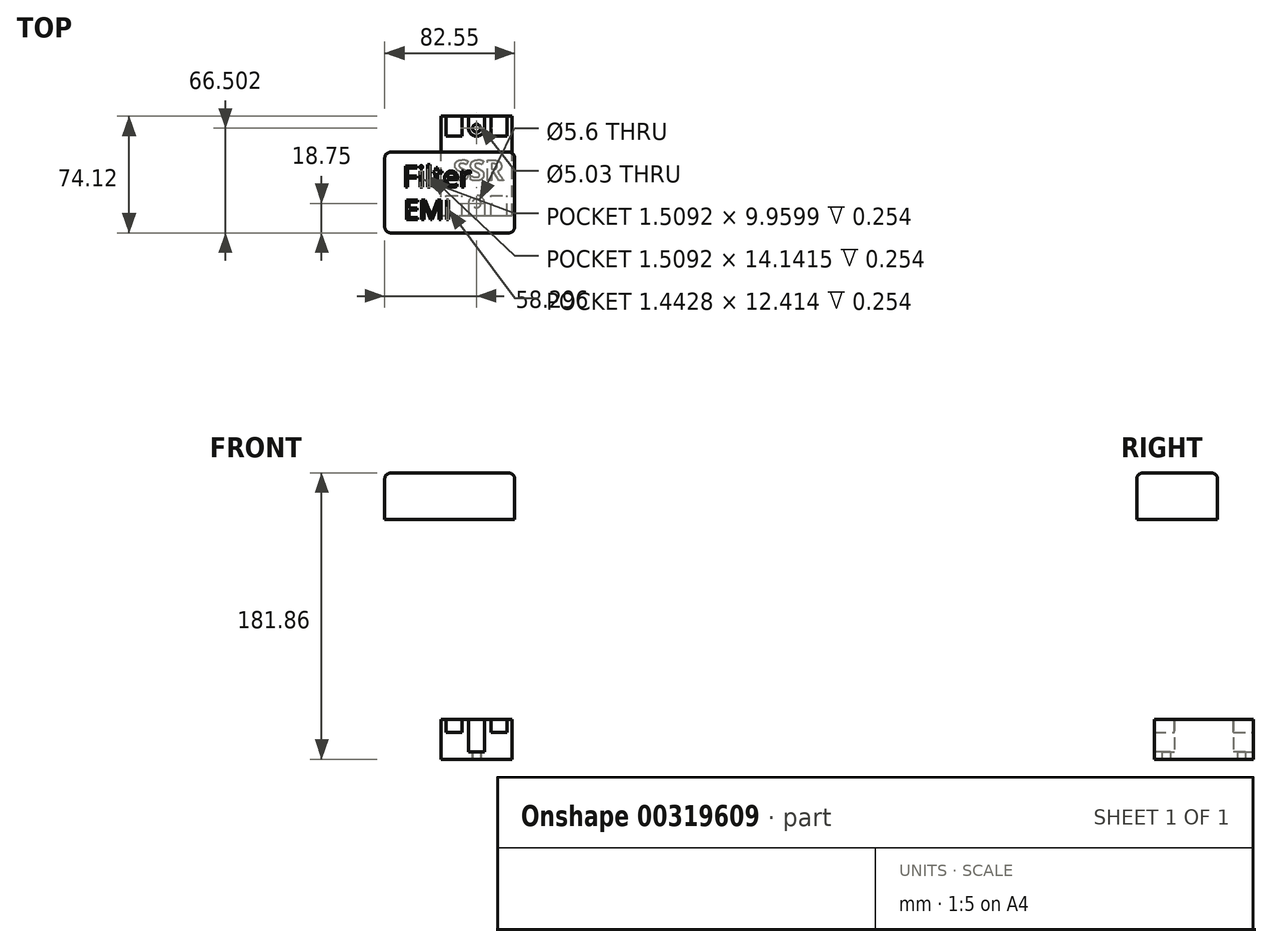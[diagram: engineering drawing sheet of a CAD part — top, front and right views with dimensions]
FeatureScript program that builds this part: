
annotation { "Feature Type Name" : "Feature", "Feature Type Description" : "" }
export const myFeature = defineFeature(function(context is Context, id is Id, definition is map)
    precondition{}
    {
        {
            var Q0;
            Q0=qCreatedBy(makeId("Top.planeOp"),FACE);
            var sketch = newSketch(context, id + "F0", { "sketchPlane" : qUnion([Q0])});
            skLineSegment(sketch, "E0.bottom", {"start": v(0, 0) * mm, "end": v(45.21, 0) * mm});
            skLineSegment(sketch, "E0.top", {"start": v(0, 63) * mm, "end": v(45.21, 63) * mm});
            skLineSegment(sketch, "E0.left", {"start": v(0, 0) * mm, "end": v(0, 63) * mm});
            skLineSegment(sketch, "E0.right", {"start": v(45.21, 0) * mm, "end": v(45.21, 63) * mm});
            skLineSegment(sketch, "E1", {"start": v(22.6, 63) * mm, "end": v(22.6, 0) * mm, "construction": true});
            skLineSegment(sketch, "E2.0", {"start": v(0, 55.37) * mm, "end": v(45.21, 55.37) * mm, "construction": true});
            skLineSegment(sketch, "E3.0", {"start": v(0, 7.62) * mm, "end": v(45.21, 7.62) * mm, "construction": true});
            skArc(sketch, "E4", {"start": v(27.69, 7.62) * mm, "mid": v(22.6, 12.7) * mm, "end": v(17.53, 7.62) * mm});
            skArc(sketch, "E5", {"start": v(17.53, 55.37) * mm, "mid": v(22.6, 50.3) * mm, "end": v(27.69, 55.37) * mm});
            skLineSegment(sketch, "E6", {"start": v(27.69, 55.37) * mm, "end": v(27.69, 63) * mm});
            skLineSegment(sketch, "E7", {"start": v(17.53, 55.37) * mm, "end": v(17.53, 63) * mm});
            skLineSegment(sketch, "E8", {"start": v(27.69, 7.62) * mm, "end": v(27.69, 0) * mm});
            skLineSegment(sketch, "E9", {"start": v(17.53, 7.62) * mm, "end": v(17.53, 0) * mm});
            skCircle(sketch, "E10", {"center": v(22.6, 55.37) * mm, "radius": 2.51 * mm});
            skCircle(sketch, "E11", {"center": v(22.6, 7.62) * mm, "radius": 2.8 * mm});
            skSolve(sketch);
        }
        {
            var Q0;
            {var subQ2=sQuery(id+"F0.wireOp",EDGE,"E0.left");Q0=makeQuery(id+"F0.imprint","IMPRINT",FACE,{"disambiguationData":[TD([[makeQuery(id+"F0.imprint","IMPRINT",EDGE,{"derivedFrom":subQ2}),-1.0]])]});}
            extrude(context, id + "F1", {"entities" : qUnion([Q0]), "depth" : 25.4 * mm});
        }
        {
            var Q0;
            Q0=makeQuery(id+"F0.imprint","IMPRINT",FACE,{"disambiguationData":[TD([[makeQuery(id+"F0.imprint","IMPRINT",EDGE,{"derivedFrom":sQuery(id+"F0.wireOp",EDGE,"E4")}),1.0]])]});
            var Q1;
            Q1=makeQuery(id+"F0.imprint","IMPRINT",FACE,{"disambiguationData":[TD([[makeQuery(id+"F0.imprint","IMPRINT",EDGE,{"derivedFrom":sQuery(id+"F0.wireOp",EDGE,"E5")}),1.0]])]});
            extrude(context, id + "F2", {"entities" : qUnion([Q0, Q1]), "operationType" : NewBodyOperationType.ADD, "depth" : 4.57 * mm});
        }
        {
            var Q0;
            Q0=makeQuery(id+"F1.opExtrude","CAP_FACE",FACE,{"disambiguationData":[OSD([sQuery(id+"F0.wireOp",EDGE,"E0.bottom"),sQuery(id+"F0.wireOp",EDGE,"E0.top"),sQuery(id+"F0.wireOp",EDGE,"E0.left"),sQuery(id+"F0.wireOp",EDGE,"E0.right"),sQuery(id+"F0.wireOp",EDGE,"E4"),sQuery(id+"F0.wireOp",EDGE,"E5"),sQuery(id+"F0.wireOp",EDGE,"E6"),sQuery(id+"F0.wireOp",EDGE,"E7"),sQuery(id+"F0.wireOp",EDGE,"E8"),sQuery(id+"F0.wireOp",EDGE,"E9")])],"isStart":false});
            var sketch = newSketch(context, id + "F3", { "sketchPlane" : qUnion([Q0])});
            skLineSegment(sketch, "E12.0", {"start": v(45.21, 0) * mm, "end": v(45.21, 63) * mm});
            skLineSegment(sketch, "E13.0", {"start": v(0, 0) * mm, "end": v(0, 63) * mm});
            skLineSegment(sketch, "E14.0", {"start": v(0, 0) * mm, "end": v(17.53, 0) * mm});
            skLineSegment(sketch, "E15.0", {"start": v(27.69, 0) * mm, "end": v(45.21, 0) * mm});
            skLineSegment(sketch, "E16.0", {"start": v(27.69, 63) * mm, "end": v(45.21, 63) * mm});
            skLineSegment(sketch, "E17.0", {"start": v(0, 63) * mm, "end": v(17.53, 63) * mm});
            skLineSegment(sketch, "E18.0", {"start": v(3.3, 0) * mm, "end": v(3.3, 12.7) * mm});
            skLineSegment(sketch, "E19.0", {"start": v(41.91, 0) * mm, "end": v(41.91, 12.7) * mm});
            skLineSegment(sketch, "E20.0", {"start": v(13.46, 0) * mm, "end": v(13.46, 12.7) * mm});
            skLineSegment(sketch, "E21.0", {"start": v(31.75, 0) * mm, "end": v(31.75, 12.7) * mm});
            skLineSegment(sketch, "E22.0", {"start": v(31.75, 12.7) * mm, "end": v(41.91, 12.7) * mm});
            skLineSegment(sketch, "E23.0", {"start": v(3.3, 12.7) * mm, "end": v(13.46, 12.7) * mm});
            skLineSegment(sketch, "E24.0", {"start": v(3.3, 50.3) * mm, "end": v(13.46, 50.3) * mm});
            skLineSegment(sketch, "E25.0", {"start": v(31.75, 50.3) * mm, "end": v(41.9, 50.3) * mm});
            skLineSegment(sketch, "E26.trimOffspring", {"start": v(41.9, 50.3) * mm, "end": v(41.9, 63) * mm});
            skLineSegment(sketch, "E27.trimOffspring", {"start": v(31.75, 50.3) * mm, "end": v(31.75, 63) * mm});
            skLineSegment(sketch, "E28.trimOffspring", {"start": v(13.46, 50.3) * mm, "end": v(13.46, 63) * mm});
            skLineSegment(sketch, "E29.trimOffspring", {"start": v(3.3, 50.3) * mm, "end": v(3.3, 63) * mm});
            skText(sketch, "E30", { "text": "SSR\n", "fontName": "OpenSans-Bold.ttf"});
            const initialGuessF3  = {"E30": [0.00792, 0.02215, 1, 0, 0.01303]};
            skSetInitialGuess(sketch, initialGuessF3);
            skSolve(sketch);
        }
        {
            var Q0;
            {var subQ0=sQuery(id+"F3.wireOp",EDGE,"E19.0");Q0=makeQuery(id+"F3.imprint","IMPRINT",FACE,{"disambiguationData":[TD([[makeQuery(id+"F3.imprint","IMPRINT",EDGE,{"derivedFrom":subQ0}),1.0]])]});}
            var Q1;
            {var subQ0=sQuery(id+"F3.wireOp",EDGE,"E18.0");Q1=makeQuery(id+"F3.imprint","IMPRINT",FACE,{"disambiguationData":[TD([[makeQuery(id+"F3.imprint","IMPRINT",EDGE,{"derivedFrom":subQ0}),-1.0]])]});}
            var Q2;
            Q2=makeQuery(id+"F3.imprint","IMPRINT",FACE,{"disambiguationData":[TD([[makeQuery(id+"F3.imprint","IMPRINT",EDGE,{"derivedFrom":sQuery(id+"F3.wireOp",EDGE,"E24.0")}),1.0]])]});
            var Q3;
            Q3=makeQuery(id+"F3.imprint","IMPRINT",FACE,{"disambiguationData":[TD([[makeQuery(id+"F3.imprint","IMPRINT",EDGE,{"derivedFrom":sQuery(id+"F3.wireOp",EDGE,"E25.0")}),1.0]])]});
            extrude(context, id + "F4", {"entities" : qUnion([Q0, Q1, Q2, Q3]), "operationType" : NewBodyOperationType.REMOVE, "oppositeDirection" : true, "depth" : 8.38 * mm});
        }
        {
            var Q0;
            Q0=makeQuery(id+"F3.imprint","IMPRINT",FACE,{"disambiguationData":[TD([[makeQuery(id+"F3.imprint","IMPRINT",EDGE,{"derivedFrom":sQuery(id+"F3.wireOp",EDGE,"E30.sketch_text.stroke-56")}),-1.0]])]});
            var Q1;
            Q1=makeQuery(id+"F3.imprint","IMPRINT",FACE,{"disambiguationData":[TD([[makeQuery(id+"F3.imprint","IMPRINT",EDGE,{"derivedFrom":sQuery(id+"F3.wireOp",EDGE,"E30.sketch_text.stroke-28")}),-1.0]])]});
            var Q2;
            Q2=makeQuery(id+"F3.imprint","IMPRINT",FACE,{"disambiguationData":[TD([[makeQuery(id+"F3.imprint","IMPRINT",EDGE,{"derivedFrom":sQuery(id+"F3.wireOp",EDGE,"E30.sketch_text.stroke-0")}),-1.0]])]});
            extrude(context, id + "F5", {"entities" : qUnion([Q0, Q1, Q2]), "operationType" : NewBodyOperationType.REMOVE, "oppositeDirection" : true, "depth" : 0.25 * mm});
        }
        {
            var Q0;
            Q0=qCreatedBy(makeId("Top.planeOp"),FACE);
            cPlane(context, id + "F6", {"entities" : qUnion([Q0]), "cplaneType" : CPlaneType.OFFSET, "offset" : 152.4 * mm, "width" : 152.4 * mm, "height" : 152.4 * mm});
        }
        {
            var Q0;
            Q0=qCreatedBy(id+"F6.planeOp",FACE);
            var sketch = newSketch(context, id + "F7", { "sketchPlane" : qUnion([Q0])});
            skLineSegment(sketch, "E31.bottom", {"start": v(-35.69, 40.18) * mm, "end": v(46.86, 40.18) * mm});
            skLineSegment(sketch, "E31.top", {"start": v(-35.69, -11.13) * mm, "end": v(46.86, -11.13) * mm});
            skLineSegment(sketch, "E31.left", {"start": v(-35.69, 40.18) * mm, "end": v(-35.69, -11.13) * mm});
            skLineSegment(sketch, "E31.right", {"start": v(46.86, 40.18) * mm, "end": v(46.86, -11.13) * mm});
            skSolve(sketch);
        }
        {
            var Q0;
            Q0=makeQuery(id+"F7.imprint","IMPRINT",FACE,{"disambiguationData":[TD([[makeQuery(id+"F7.imprint","IMPRINT",EDGE,{"derivedFrom":sQuery(id+"F7.wireOp",EDGE,"E31.bottom")}),-1.0]])]});
            extrude(context, id + "F8", {"entities" : qUnion([Q0]), "depth" : 29.46 * mm});
        }
        {
            var Q0;
            Q0=makeQuery(id+"F8.opExtrude","CAP_EDGE",EDGE,{"disambiguationData":[OSD([sQuery(id+"F7.wireOp",EDGE,"E31.top")])],"isStart":false});
            var Q1;
            Q1=makeQuery(id+"F8.opExtrude","CAP_EDGE",EDGE,{"disambiguationData":[OSD([sQuery(id+"F7.wireOp",EDGE,"E31.right")])],"isStart":false});
            var Q2;
            Q2=makeQuery(id+"F8.opExtrude","CAP_EDGE",EDGE,{"disambiguationData":[OSD([sQuery(id+"F7.wireOp",EDGE,"E31.bottom")])],"isStart":false});
            var Q3;
            Q3=makeQuery(id+"F8.opExtrude","SWEPT_EDGE",EDGE,{"disambiguationData":[OSD([sQuery(id+"F7.wireOp",EDGE,"E31.bottom"),sQuery(id+"F7.wireOp",EDGE,"E31.right")])]});
            var Q4;
            Q4=makeQuery(id+"F8.opExtrude","SWEPT_EDGE",EDGE,{"disambiguationData":[OSD([sQuery(id+"F7.wireOp",EDGE,"E31.bottom"),sQuery(id+"F7.wireOp",EDGE,"E31.left")])]});
            var Q5;
            Q5=makeQuery(id+"F8.opExtrude","SWEPT_EDGE",EDGE,{"disambiguationData":[OSD([sQuery(id+"F7.wireOp",EDGE,"E31.top"),sQuery(id+"F7.wireOp",EDGE,"E31.right")])]});
            var Q6;
            Q6=makeQuery(id+"F8.opExtrude","CAP_EDGE",EDGE,{"disambiguationData":[OSD([sQuery(id+"F7.wireOp",EDGE,"E31.left")])],"isStart":false});
            var Q7;
            Q7=makeQuery(id+"F8.opExtrude","SWEPT_EDGE",EDGE,{"disambiguationData":[OSD([sQuery(id+"F7.wireOp",EDGE,"E31.top"),sQuery(id+"F7.wireOp",EDGE,"E31.left")])]});
            fillet(context, id + "F9", {"entities" : qUnion([Q0, Q1, Q2, Q3, Q4, Q5, Q6, Q7]), "radius" : 3.8 * mm, "tangentPropagation" : true, "allowEdgeOverflow" : false});
        }
        {
            var Q0;
            Q0=makeQuery(id+"F8.opExtrude","CAP_FACE",FACE,{"disambiguationData":[OSD([sQuery(id+"F7.wireOp",EDGE,"E31.bottom"),sQuery(id+"F7.wireOp",EDGE,"E31.top"),sQuery(id+"F7.wireOp",EDGE,"E31.left"),sQuery(id+"F7.wireOp",EDGE,"E31.right")])],"isStart":false});
            var sketch = newSketch(context, id + "F10", { "sketchPlane" : qUnion([Q0])});
            skText(sketch, "E32", { "text": "Filter\n", "fontName": "OpenSans-Regular.ttf"});
            skText(sketch, "E33", { "text": "EMI", "fontName": "OpenSans-Regular.ttf"});
            const initialGuessF10  = {"E32": [-0.02444, 0.01803, 1, 0, 0.0134], "E33": [-0.02354, -0.00253, 1, 0, 0.01252]};
            skSetInitialGuess(sketch, initialGuessF10);
            skSolve(sketch);
        }
        {
            var Q0;
            Q0=qSketchRegion(id+"F10",true);
            extrude(context, id + "F11", {"entities" : qUnion([Q0]), "operationType" : NewBodyOperationType.REMOVE, "oppositeDirection" : true, "depth" : 0.25 * mm});
        }
    });
